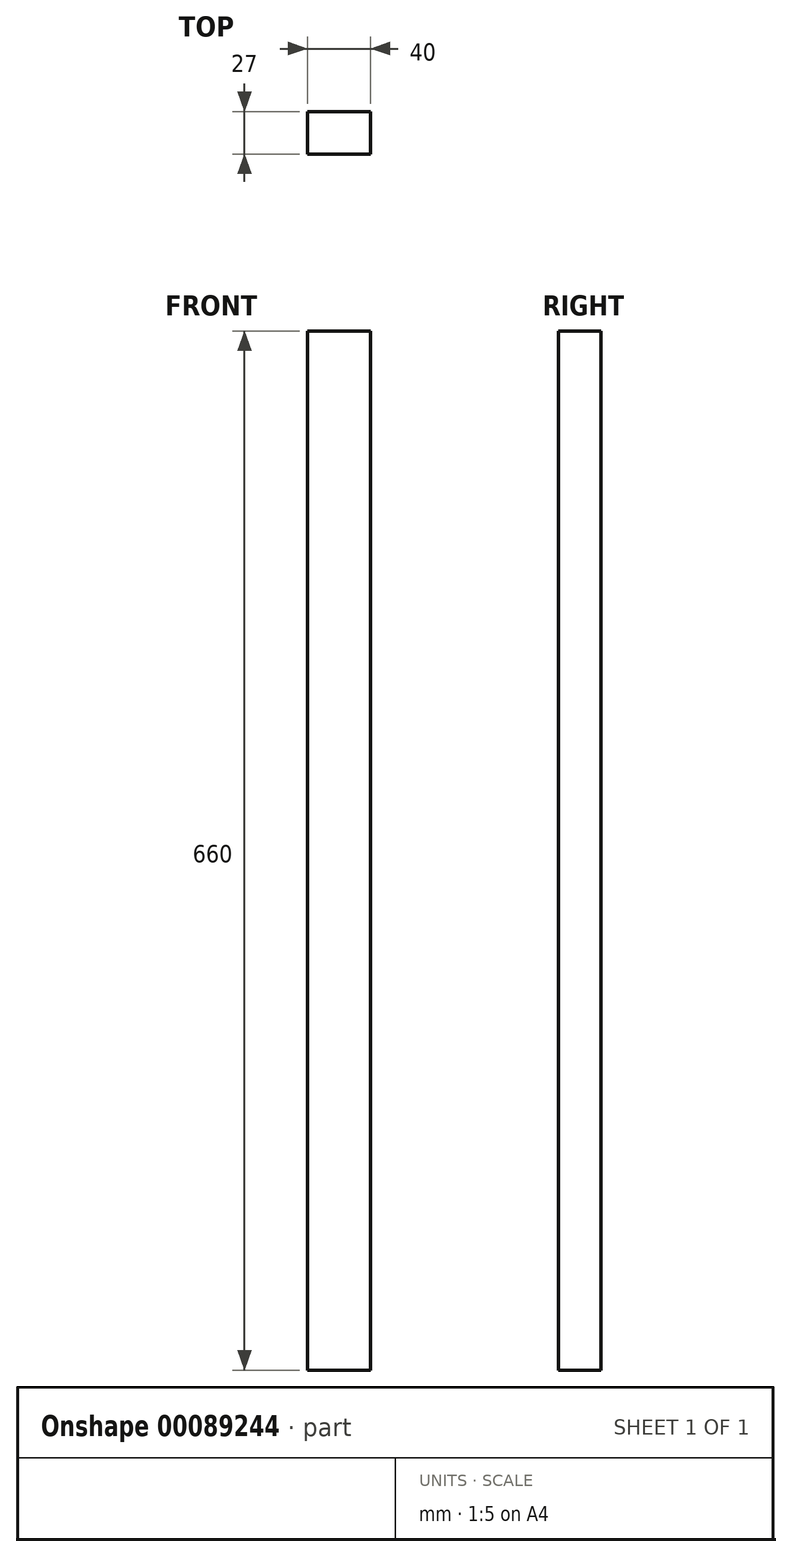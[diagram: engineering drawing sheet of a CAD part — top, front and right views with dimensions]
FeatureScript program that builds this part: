
annotation { "Feature Type Name" : "Feature", "Feature Type Description" : "" }
export const myFeature = defineFeature(function(context is Context, id is Id, definition is map)
    precondition{}
    {
        {
            var Q0;
            Q0=qCreatedBy(makeId("Top.planeOp"),FACE);
            var sketch = newSketch(context, id + "F0", { "sketchPlane" : qUnion([Q0])});
            skLineSegment(sketch, "E0.bottom", {"start": v(-20, 13.5) * mm, "end": v(20, 13.5) * mm});
            skLineSegment(sketch, "E0.top", {"start": v(-20, -13.5) * mm, "end": v(20, -13.5) * mm});
            skLineSegment(sketch, "E0.left", {"start": v(-20, 13.5) * mm, "end": v(-20, -13.5) * mm});
            skLineSegment(sketch, "E0.right", {"start": v(20, 13.5) * mm, "end": v(20, -13.5) * mm});
            skPoint(sketch, "E0.middle", {"position": v(0, 0) * mm});
            skSolve(sketch);
        }
        {
            var Q0;
            Q0=makeQuery(id+"F0.imprint","IMPRINT",FACE,{"disambiguationData":[TD([[makeQuery(id+"F0.imprint","IMPRINT",EDGE,{"derivedFrom":sQuery(id+"F0.wireOp",EDGE,"E0.bottom")}),-1.0]])]});
            extrude(context, id + "F1", {"entities" : qUnion([Q0]), "depth" : 660 * mm});
        }
    });
